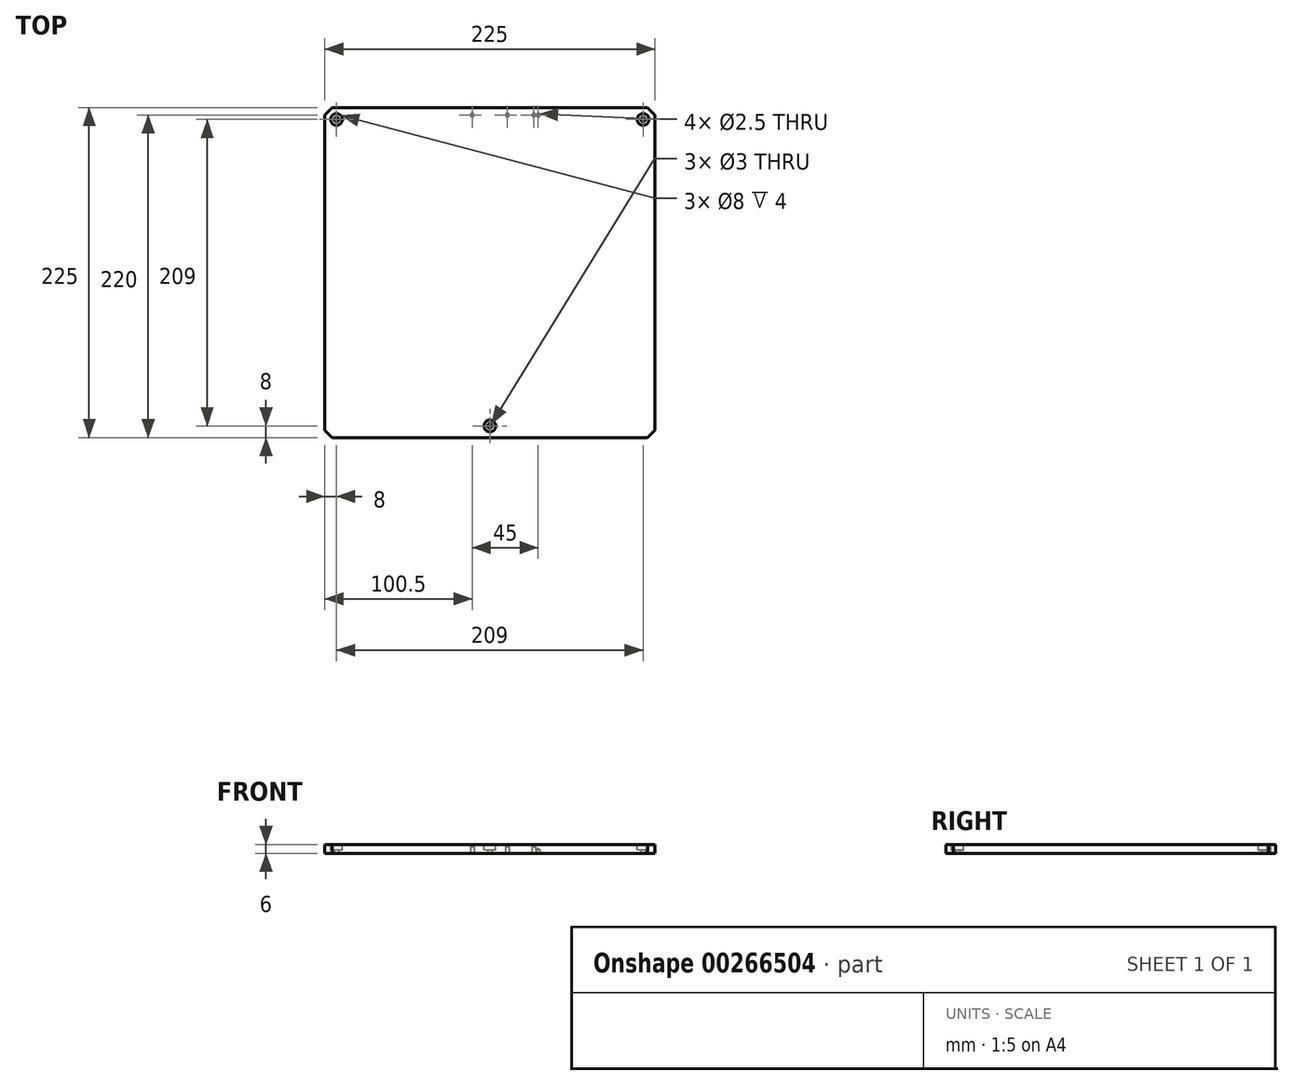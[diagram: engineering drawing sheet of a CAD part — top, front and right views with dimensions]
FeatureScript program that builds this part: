
annotation { "Feature Type Name" : "Feature", "Feature Type Description" : "" }
export const myFeature = defineFeature(function(context is Context, id is Id, definition is map)
    precondition{}
    {
        {
            var Q0;
            Q0=qCreatedBy(makeId("Top.planeOp"),FACE);
            var sketch = newSketch(context, id + "F0", { "sketchPlane" : qUnion([Q0])});
            skLineSegment(sketch, "E0.bottom", {"start": v(0, 0) * mm, "end": v(225, 0) * mm});
            skLineSegment(sketch, "E0.top", {"start": v(0, 225) * mm, "end": v(225, 225) * mm});
            skLineSegment(sketch, "E0.left", {"start": v(0, 0) * mm, "end": v(0, 225) * mm});
            skLineSegment(sketch, "E0.right", {"start": v(225, 0) * mm, "end": v(225, 225) * mm});
            skLineSegment(sketch, "E1", {"start": v(0, 225) * mm, "end": v(225, 0) * mm, "construction": true});
            skLineSegment(sketch, "E2", {"start": v(0, 0) * mm, "end": v(225, 225) * mm, "construction": true});
            skLineSegment(sketch, "E3", {"start": v(112.5, 225) * mm, "end": v(112.5, 0) * mm, "construction": true});
            skCircle(sketch, "E4", {"center": v(8, 217) * mm, "radius": 1.5 * mm});
            skCircle(sketch, "E5", {"center": v(217, 217) * mm, "radius": 1.5 * mm});
            skCircle(sketch, "E6", {"center": v(112.5, 8) * mm, "radius": 1.5 * mm});
            skSolve(sketch);
        }
        {
            var Q0;
            Q0 = qSketchRegion(id + "F0", true);
            extrude(context, id + "F1", {"entities" : qUnion([Q0]), "depth" : 6 * mm});
        }
        {
            var Q0;
            Q0=makeQuery(id+"F1.opExtrude","CAP_FACE",FACE,{"disambiguationData":[OSD([sQuery(id+"F0.wireOp",EDGE,"E0.bottom"),sQuery(id+"F0.wireOp",EDGE,"E0.top"),sQuery(id+"F0.wireOp",EDGE,"E0.left"),sQuery(id+"F0.wireOp",EDGE,"E0.right"),sQuery(id+"F0.wireOp",EDGE,"E4"),sQuery(id+"F0.wireOp",EDGE,"E5"),sQuery(id+"F0.wireOp",EDGE,"Zo3WfQfq-pkXe-2Bfn-fg5S-mHa09XyBqBsQ"),sQuery(id+"F0.wireOp",EDGE,"XlddhZ3R-kbGH-BxdO-0Tjn-xPMr2SYzn92N"),sQuery(id+"F0.wireOp",EDGE,"E6")])],"isStart":false});
            var sketch = newSketch(context, id + "F2", { "sketchPlane" : qUnion([Q0])});
            skCircle(sketch, "E7", {"center": v(112.5, 8) * mm, "radius": 4 * mm});
            skCircle(sketch, "E8", {"center": v(8, 217) * mm, "radius": 4 * mm});
            skCircle(sketch, "E9", {"center": v(217, 217) * mm, "radius": 4 * mm});
            skSolve(sketch);
        }
        {
            var Q0;
            Q0 = qSketchRegion(id + "F2", true);
            extrude(context, id + "F3", {"entities" : qUnion([Q0]), "operationType" : NewBodyOperationType.REMOVE, "oppositeDirection" : true, "depth" : 4 * mm});
        }
        {
            var Q0;
            Q0=makeQuery(id+"F1.opExtrude","SWEPT_EDGE",EDGE,{"disambiguationData":[OSD([sQuery(id+"F0.wireOp",EDGE,"E0.bottom"),sQuery(id+"F0.wireOp",EDGE,"E0.right")])]});
            var Q1;
            Q1=makeQuery(id+"F1.opExtrude","SWEPT_EDGE",EDGE,{"disambiguationData":[OSD([sQuery(id+"F0.wireOp",EDGE,"E0.bottom"),sQuery(id+"F0.wireOp",EDGE,"E0.left")])]});
            var Q2;
            Q2=makeQuery(id+"F1.opExtrude","SWEPT_EDGE",EDGE,{"disambiguationData":[OSD([sQuery(id+"F0.wireOp",EDGE,"E0.top"),sQuery(id+"F0.wireOp",EDGE,"E0.right")])]});
            var Q3;
            Q3=makeQuery(id+"F1.opExtrude","SWEPT_EDGE",EDGE,{"disambiguationData":[OSD([sQuery(id+"F0.wireOp",EDGE,"E0.top"),sQuery(id+"F0.wireOp",EDGE,"E0.left")])]});
            chamfer(context, id + "F4", {"entities" : qUnion([Q0, Q1, Q2, Q3]), "width" : 5 * mm, "tangentPropagation" : true});
        }
        {
            var Q0;
            Q0=makeQuery(id+"F1.opExtrude","CAP_FACE",FACE,{"disambiguationData":[OSD([sQuery(id+"F0.wireOp",EDGE,"E0.bottom"),sQuery(id+"F0.wireOp",EDGE,"E0.top"),sQuery(id+"F0.wireOp",EDGE,"E0.left"),sQuery(id+"F0.wireOp",EDGE,"E0.right"),sQuery(id+"F0.wireOp",EDGE,"E4"),sQuery(id+"F0.wireOp",EDGE,"E5"),sQuery(id+"F0.wireOp",EDGE,"E6")])],"isStart":true});
            var sketch = newSketch(context, id + "F5", { "sketchPlane" : qUnion([Q0])});
            skLineSegment(sketch, "E10", {"start": v(0, -220) * mm, "end": v(225, -220) * mm, "construction": true});
            skLineSegment(sketch, "E11", {"start": v(112.5, 0) * mm, "end": v(112.5, -225) * mm, "construction": true});
            skPoint(sketch, "E12", {"position": v(100.5, -220) * mm});
            skPoint(sketch, "E13", {"position": v(124.5, -220) * mm});
            skPoint(sketch, "E14", {"position": v(142.5, -220) * mm});
            skPoint(sketch, "E15", {"position": v(145.5, -220) * mm});
            skSolve(sketch);
        }
        {
            var Q0;
            Q0=sQuery(id+"F5.wireOp",VERTEX,"E12");
            var Q1;
            Q1=sQuery(id+"F5.wireOp",VERTEX,"E13");
            var Q2;
            Q2=sQuery(id+"F5.wireOp",VERTEX,"E14");
            var Q3;
            Q3=makeQuery(id+"F1.opExtrude","SWEPT_BODY",BODY,{"disambiguationData":[OSD([sQuery(id+"F0.wireOp",EDGE,"E0.bottom"),sQuery(id+"F0.wireOp",EDGE,"E0.top"),sQuery(id+"F0.wireOp",EDGE,"E0.left"),sQuery(id+"F0.wireOp",EDGE,"E0.right"),sQuery(id+"F0.wireOp",EDGE,"E4"),sQuery(id+"F0.wireOp",EDGE,"E5"),sQuery(id+"F0.wireOp",EDGE,"E6")])]});
            hole(context, id + "F6", {"style" : HoleStyle.SIMPLE, "endStyle" : HoleEndStyle.BLIND, "standardTappedOrClearance" : lookupTablePath({ "standard" : "ISO", "engagement" : "75%", "pitch" : "0.5 mm", "size" : "M3", "type" : "Tapped" }), "standardBlindInLast" : lookupTablePath({ "standard" : "ISO", "engagement" : "75%", "pitch" : "0.5 mm", "size" : "M3", "type" : "Tapped" }), "holeDiameter" : 2.5 * mm, "showTappedDepth" : true, "holeDepth" : 4.5 * mm, "tappedDepth" : 3 * mm, "tapClearance" : 3, "startFromSketch" : true, "locations" : qUnion([Q0, Q1, Q2]), "scope" : qUnion([Q3]), "majorDiameter" : 3 * mm});
        }
        {
            var Q0;
            Q0=sQuery(id+"F5.wireOp",VERTEX,"E15");
            var Q1;
            Q1=makeQuery(id+"F1.opExtrude","SWEPT_BODY",BODY,{"disambiguationData":[OSD([sQuery(id+"F0.wireOp",EDGE,"E0.bottom"),sQuery(id+"F0.wireOp",EDGE,"E0.top"),sQuery(id+"F0.wireOp",EDGE,"E0.left"),sQuery(id+"F0.wireOp",EDGE,"E0.right"),sQuery(id+"F0.wireOp",EDGE,"E4"),sQuery(id+"F0.wireOp",EDGE,"E5"),sQuery(id+"F0.wireOp",EDGE,"E6")])]});
            hole(context, id + "F7", {"style" : HoleStyle.SIMPLE, "endStyle" : HoleEndStyle.BLIND, "holeDiameter" : 2.5 * mm, "holeDepth" : 2.5 * mm, "tappedDepth" : 0.7 * mm, "tapClearance" : 3, "startFromSketch" : true, "locations" : qUnion([Q0]), "scope" : qUnion([Q1])});
        }
    });
